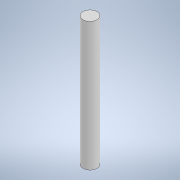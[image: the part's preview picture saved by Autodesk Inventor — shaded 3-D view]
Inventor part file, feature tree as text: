
AUTODESK INVENTOR PART (.ipt)
format: ipt  version: 2022 (Build 260153000, 153)  size: 90,624 bytes
history: native  units: mm
features: extrude x1, sketch x1
ambient origin geometry x8: Origin, YZ Plane, XZ Plane, XY Plane, X Axis, Y Axis, Z Axis, Center Point
bodies: Solid1 (feature_tree)
feature tree (2):
  extrude  "Extrusion1"  Depth=73.0mm TaperAngle=0.0deg
  sketch  "Sketch1"  dims[d0=8.0mm d1=73.0mm d2=0.0mm]
